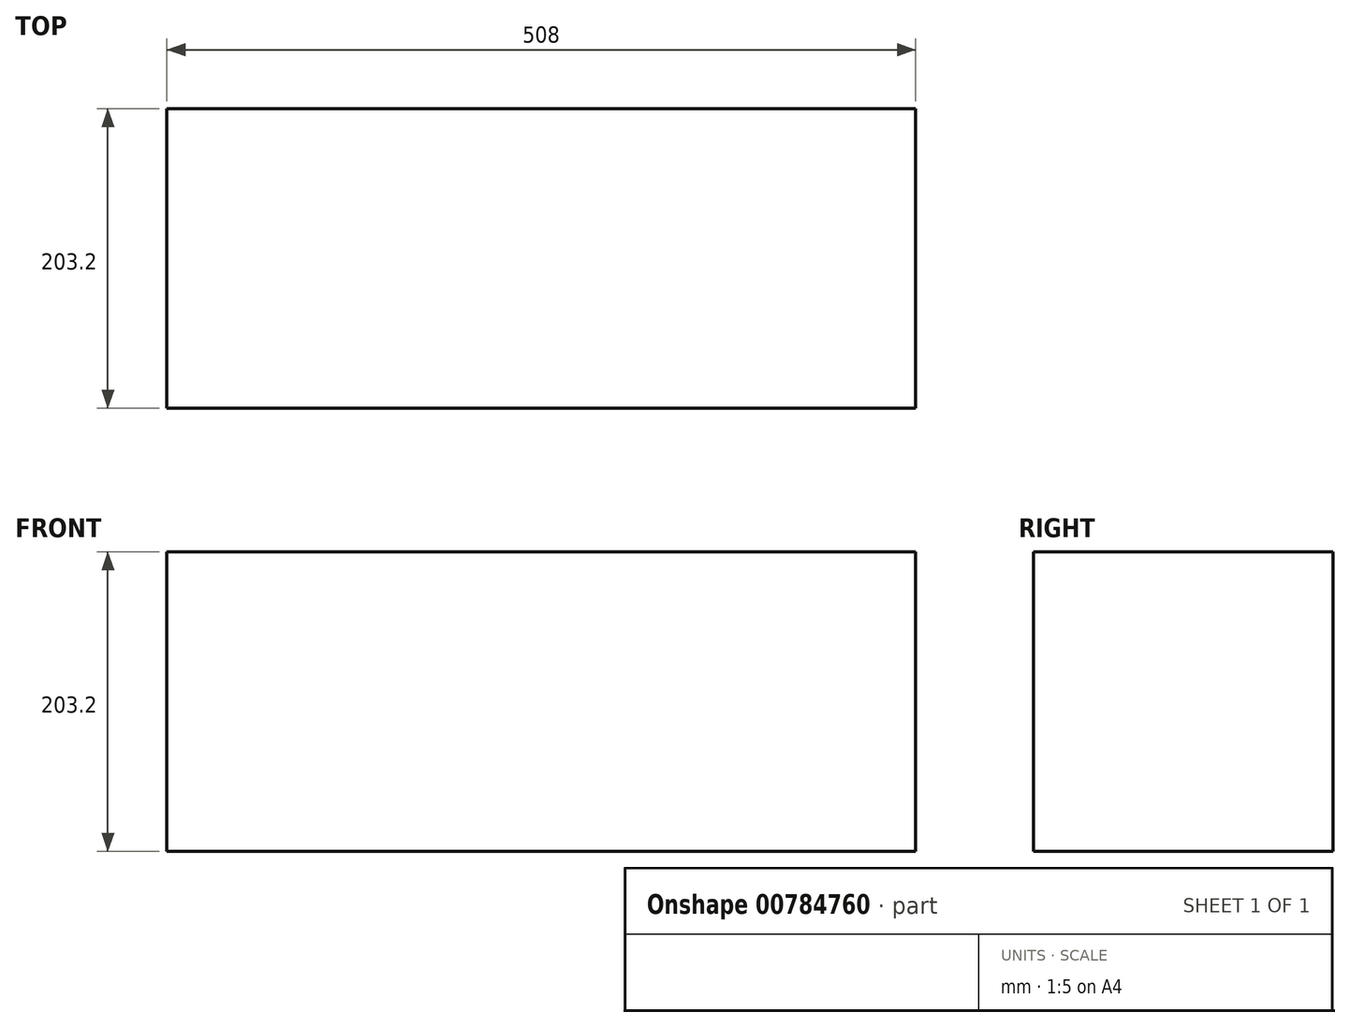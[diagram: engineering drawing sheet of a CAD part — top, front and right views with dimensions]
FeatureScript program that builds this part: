
annotation { "Feature Type Name" : "Feature", "Feature Type Description" : "" }
export const myFeature = defineFeature(function(context is Context, id is Id, definition is map)
    precondition{}
    {
        {
            var Q0;
            Q0=qCreatedBy(makeId("Front.planeOp"),FACE);
            var sketch = newSketch(context, id + "F0", { "sketchPlane" : qUnion([Q0])});
            skLineSegment(sketch, "E0.bottom", {"start": v(254, -101.6) * mm, "end": v(-254, -101.6) * mm});
            skLineSegment(sketch, "E0.top", {"start": v(254, 101.6) * mm, "end": v(-254, 101.6) * mm});
            skLineSegment(sketch, "E0.left", {"start": v(254, -101.6) * mm, "end": v(254, 101.6) * mm});
            skLineSegment(sketch, "E0.right", {"start": v(-254, -101.6) * mm, "end": v(-254, 101.6) * mm});
            skPoint(sketch, "E0.middle", {"position": v(0, 0) * mm});
            skSolve(sketch);
        }
        {
            var Q0;
            Q0 = qSketchRegion(id + "F0", true);
            extrude(context, id + "F1", {"entities" : qUnion([Q0]), "depth" : 203.2 * mm, "offsetDistance" : 25.4 * mm});
        }
    });
